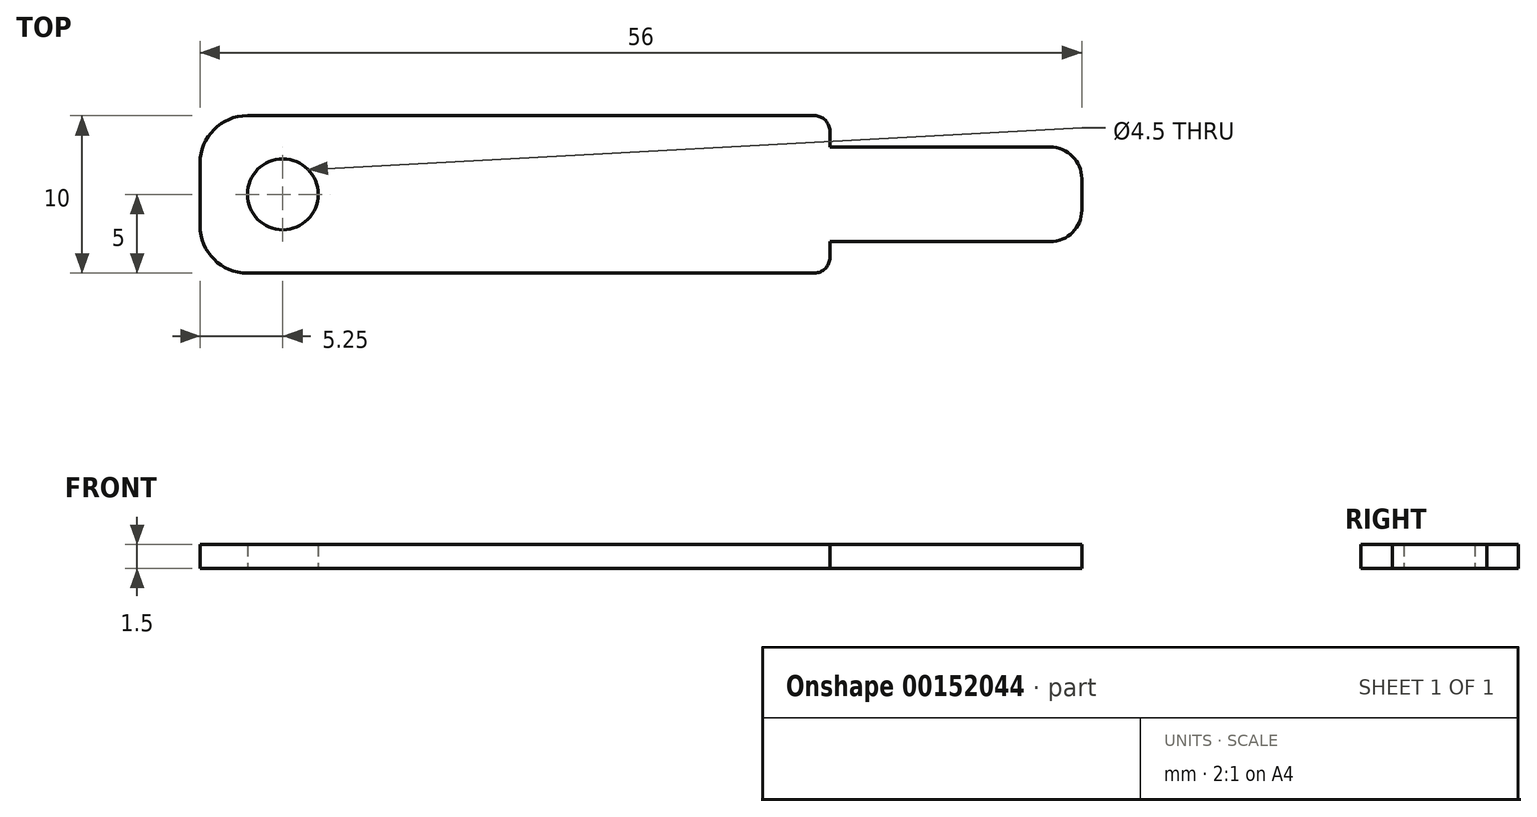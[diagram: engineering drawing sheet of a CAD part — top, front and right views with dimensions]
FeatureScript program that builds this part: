
annotation { "Feature Type Name" : "Feature", "Feature Type Description" : "" }
export const myFeature = defineFeature(function(context is Context, id is Id, definition is map)
    precondition{}
    {
        {
            var Q0;
            Q0=qCreatedBy(makeId("Top.planeOp"),FACE);
            var sketch = newSketch(context, id + "F0", { "sketchPlane" : qUnion([Q0])});
            skLineSegment(sketch, "E0.bottom", {"start": v(11, -5) * mm, "end": v(-25, -5) * mm});
            skLineSegment(sketch, "E0.top", {"start": v(12, 5) * mm, "end": v(-25, 5) * mm});
            skLineSegment(sketch, "E0.left", {"start": v(28, -3) * mm, "end": v(28, 3) * mm});
            skLineSegment(sketch, "E0.right", {"start": v(-28, -2) * mm, "end": v(-28, 2) * mm});
            skPoint(sketch, "E0.middle", {"position": v(0, 0) * mm});
            skLineSegment(sketch, "E1.bottom", {"start": v(28, 3) * mm, "end": v(12, 3) * mm});
            skLineSegment(sketch, "E1.top", {"start": v(28, -3) * mm, "end": v(12, -3) * mm});
            skLineSegment(sketch, "E1.left", {"start": v(28, 3) * mm, "end": v(28, -3) * mm});
            skLineSegment(sketch, "E1.right", {"start": v(12, 3) * mm, "end": v(12, -3) * mm});
            skLineSegment(sketch, "E2", {"start": v(12, 3) * mm, "end": v(12, 5) * mm});
            skLineSegment(sketch, "E3", {"start": v(12, 5) * mm, "end": v(12, -3) * mm});
            skLineSegment(sketch, "E4", {"start": v(12, -3) * mm, "end": v(12, -4) * mm});
            skPoint(sketch, "E5.orphan", {"position": v(28, 5) * mm});
            skPoint(sketch, "E6.orphan", {"position": v(28, -5) * mm});
            skPoint(sketch, "E7.visualSharp", {"position": v(-28, 5) * mm});
            skArc(sketch, "E7.filletArc", {"start": v(-25, 5) * mm, "mid": v(-27.12, 4.12) * mm, "end": v(-28, 2) * mm});
            skPoint(sketch, "E8.visualSharp", {"position": v(-28, -5) * mm});
            skArc(sketch, "E8.filletArc", {"start": v(-28, -2) * mm, "mid": v(-27.12, -4.12) * mm, "end": v(-25, -5) * mm});
            skPoint(sketch, "E9.visualSharp", {"position": v(12, -5) * mm});
            skArc(sketch, "E9.filletArc", {"start": v(11, -5) * mm, "mid": v(11.7, -4.7) * mm, "end": v(12, -4) * mm});
            skCircle(sketch, "E10", {"center": v(-22.75, 0) * mm, "radius": 2.25 * mm});
            skSolve(sketch);
        }
        {
            var Q0;
            Q0 = qSketchRegion(id + "F0", true);
            extrude(context, id + "F1", {"entities" : qUnion([Q0]), "depth" : 1.5 * mm});
        }
        {
            var Q0;
            Q0=makeQuery(id+"F1.opExtrude","SWEPT_EDGE",EDGE,{"disambiguationData":[OSD([sQuery(id+"F0.wireOp",EDGE,"E0.top"),sQuery(id+"F0.wireOp",EDGE,"E3")])]});
            fillet(context, id + "F2", {"entities" : qUnion([Q0]), "radius" : 1 * mm, "tangentPropagation" : true, "allowEdgeOverflow" : false});
        }
        {
            var Q0;
            Q0=makeQuery(id+"F1.opExtrude","SWEPT_EDGE",EDGE,{"disambiguationData":[OSD([sQuery(id+"F0.wireOp",EDGE,"E1.bottom"),sQuery(id+"F0.wireOp",EDGE,"E1.left")])]});
            var Q1;
            Q1=makeQuery(id+"F1.opExtrude","SWEPT_EDGE",EDGE,{"disambiguationData":[OSD([sQuery(id+"F0.wireOp",EDGE,"E1.top"),sQuery(id+"F0.wireOp",EDGE,"E1.left")])]});
            fillet(context, id + "F3", {"entities" : qUnion([Q0, Q1]), "radius" : 2 * mm, "tangentPropagation" : true, "allowEdgeOverflow" : false});
        }
    });
